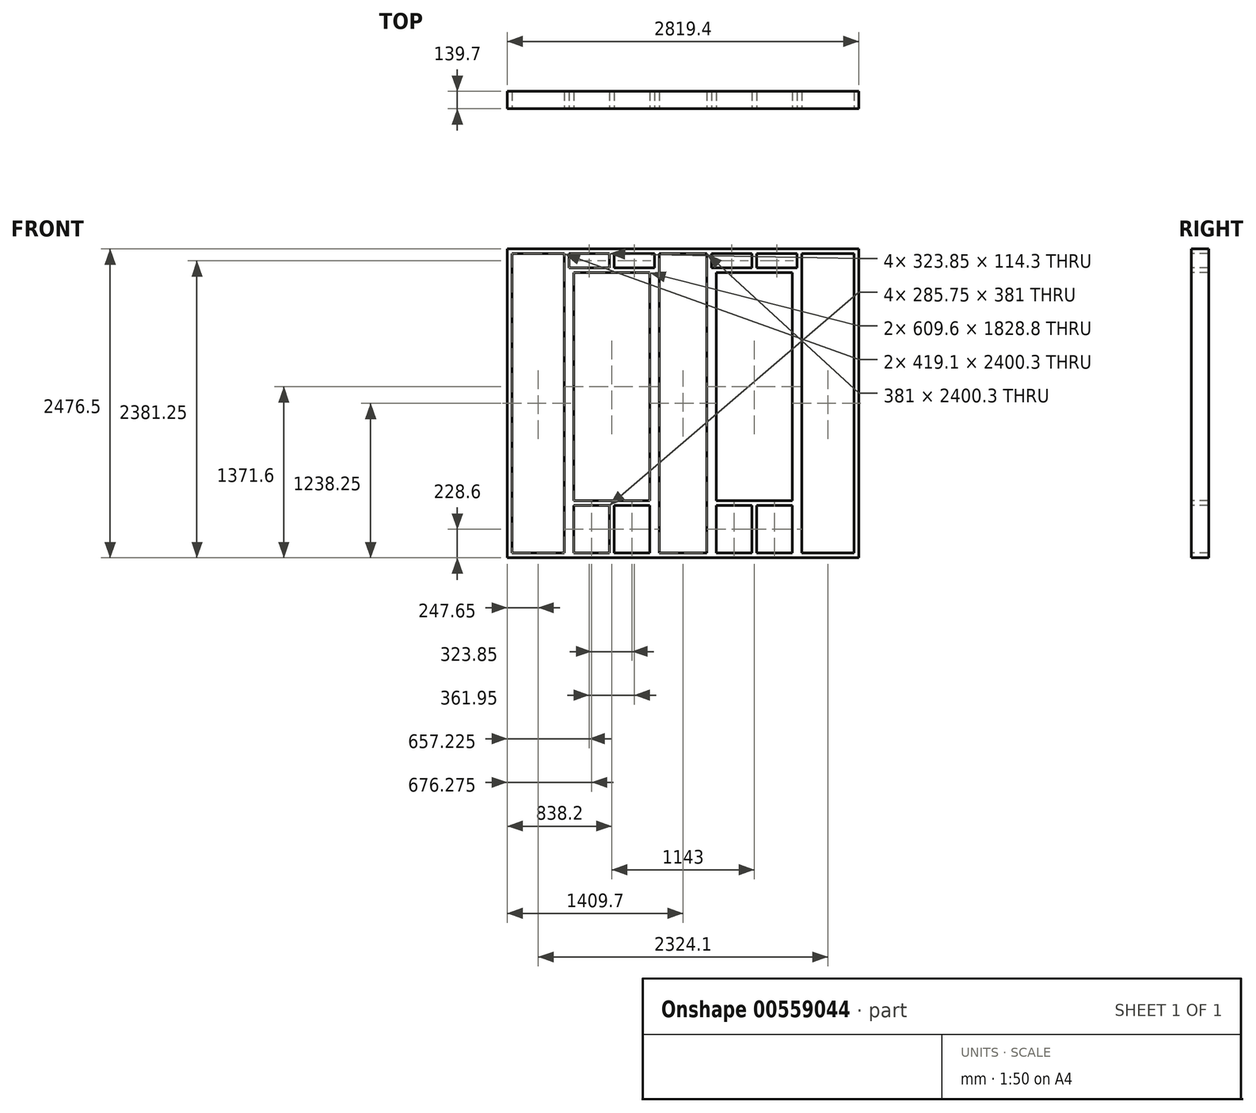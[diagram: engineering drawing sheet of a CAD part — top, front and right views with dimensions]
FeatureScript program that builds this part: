
annotation { "Feature Type Name" : "Feature", "Feature Type Description" : "" }
export const myFeature = defineFeature(function(context is Context, id is Id, definition is map)
    precondition{}
    {
        {
            var Q0;
            Q0=qCreatedBy(makeId("Front.planeOp"),FACE);
            var sketch = newSketch(context, id + "F0", { "sketchPlane" : qUnion([Q0])});
            skLineSegment(sketch, "E0.bottom", {"start": v(0, 0) * mm, "end": v(2819.4, 0) * mm});
            skLineSegment(sketch, "E0.top", {"start": v(0, 2476.5) * mm, "end": v(2819.4, 2476.5) * mm});
            skLineSegment(sketch, "E0.left", {"start": v(0, 0) * mm, "end": v(0, 2476.5) * mm});
            skLineSegment(sketch, "E0.right", {"start": v(2819.4, 0) * mm, "end": v(2819.4, 2476.5) * mm});
            skSolve(sketch);
        }
        {
            var Q0;
            Q0 = qSketchRegion(id + "F0", true);
            extrude(context, id + "F1", {"entities" : qUnion([Q0]), "depth" : 139.7 * mm, "offsetDistance" : 25.4 * mm});
        }
        {
            var Q0;
            Q0=makeQuery(id+"F1.opExtrude","CAP_FACE",FACE,{"disambiguationData":[OSD([sQuery(id+"F0.wireOp",EDGE,"E0.bottom"),sQuery(id+"F0.wireOp",EDGE,"E0.top"),sQuery(id+"F0.wireOp",EDGE,"E0.left"),sQuery(id+"F0.wireOp",EDGE,"E0.right")])],"isStart":false});
            var sketch = newSketch(context, id + "F2", { "sketchPlane" : qUnion([Q0])});
            skLineSegment(sketch, "E1.bottom", {"start": v(533.4, 457.2) * mm, "end": v(1143, 457.2) * mm});
            skLineSegment(sketch, "E1.top", {"start": v(533.4, 2286) * mm, "end": v(1143, 2286) * mm});
            skLineSegment(sketch, "E1.left", {"start": v(533.4, 457.2) * mm, "end": v(533.4, 2286) * mm});
            skLineSegment(sketch, "E1.right", {"start": v(1143, 457.2) * mm, "end": v(1143, 2286) * mm});
            skLineSegment(sketch, "E2.bottom", {"start": v(1676.4, 457.2) * mm, "end": v(2286, 457.2) * mm});
            skLineSegment(sketch, "E2.top", {"start": v(1676.4, 2286) * mm, "end": v(2286, 2286) * mm});
            skLineSegment(sketch, "E2.left", {"start": v(1676.4, 457.2) * mm, "end": v(1676.4, 2286) * mm});
            skLineSegment(sketch, "E2.right", {"start": v(2286, 457.2) * mm, "end": v(2286, 2286) * mm});
            skLineSegment(sketch, "E3", {"start": v(533.4, 2286) * mm, "end": v(0, 2286) * mm, "construction": true});
            skLineSegment(sketch, "E4", {"start": v(1143, 2286) * mm, "end": v(1676.4, 2286) * mm, "construction": true});
            skLineSegment(sketch, "E5", {"start": v(2286, 2286) * mm, "end": v(2819.4, 2286) * mm, "construction": true});
            skSolve(sketch);
        }
        {
            var Q0;
            Q0 = qSketchRegion(id + "F2", true);
            extrude(context, id + "F3", {"entities" : qUnion([Q0]), "operationType" : NewBodyOperationType.REMOVE, "endBound" : BoundingType.THROUGH_ALL, "oppositeDirection" : true, "depth" : 25.4 * mm, "offsetDistance" : 25.4 * mm});
        }
        {
            var Q0;
            Q0=makeQuery(id+"F1.opExtrude","CAP_FACE",FACE,{"disambiguationData":[OSD([sQuery(id+"F0.wireOp",EDGE,"E0.bottom"),sQuery(id+"F0.wireOp",EDGE,"E0.top"),sQuery(id+"F0.wireOp",EDGE,"E0.left"),sQuery(id+"F0.wireOp",EDGE,"E0.right")])],"isStart":false});
            var sketch = newSketch(context, id + "F4", { "sketchPlane" : qUnion([Q0])});
            skLineSegment(sketch, "E6.bottom", {"start": v(2781.3, 38.1) * mm, "end": v(2362.2, 38.1) * mm});
            skLineSegment(sketch, "E6.top", {"start": v(2781.3, 2438.4) * mm, "end": v(2362.2, 2438.4) * mm});
            skLineSegment(sketch, "E6.left", {"start": v(2781.3, 38.1) * mm, "end": v(2781.3, 2438.4) * mm});
            skLineSegment(sketch, "E6.right", {"start": v(2362.2, 38.1) * mm, "end": v(2362.2, 2438.4) * mm});
            skLineSegment(sketch, "E7.bottom", {"start": v(1600.2, 2438.4) * mm, "end": v(1219.2, 2438.4) * mm});
            skLineSegment(sketch, "E7.top", {"start": v(1600.2, 38.1) * mm, "end": v(1219.2, 38.1) * mm});
            skLineSegment(sketch, "E7.left", {"start": v(1600.2, 2438.4) * mm, "end": v(1600.2, 38.1) * mm});
            skLineSegment(sketch, "E7.right", {"start": v(1219.2, 2438.4) * mm, "end": v(1219.2, 38.1) * mm});
            skLineSegment(sketch, "E8.bottom", {"start": v(457.2, 2438.4) * mm, "end": v(38.1, 2438.4) * mm});
            skLineSegment(sketch, "E8.top", {"start": v(457.2, 38.1) * mm, "end": v(38.1, 38.1) * mm});
            skLineSegment(sketch, "E8.left", {"start": v(457.2, 2438.4) * mm, "end": v(457.2, 38.1) * mm});
            skLineSegment(sketch, "E8.right", {"start": v(38.1, 2438.4) * mm, "end": v(38.1, 38.1) * mm});
            skLineSegment(sketch, "E9.bottom", {"start": v(495.3, 2324.1) * mm, "end": v(819.15, 2324.1) * mm});
            skLineSegment(sketch, "E9.top", {"start": v(495.3, 2438.4) * mm, "end": v(819.15, 2438.4) * mm});
            skLineSegment(sketch, "E9.left", {"start": v(495.3, 2324.1) * mm, "end": v(495.3, 2438.4) * mm});
            skLineSegment(sketch, "E9.right", {"start": v(819.15, 2324.1) * mm, "end": v(819.15, 2438.4) * mm});
            skLineSegment(sketch, "E10.bottom", {"start": v(1181.1, 2324.1) * mm, "end": v(857.25, 2324.1) * mm});
            skLineSegment(sketch, "E10.top", {"start": v(1181.1, 2438.4) * mm, "end": v(857.25, 2438.4) * mm});
            skLineSegment(sketch, "E10.left", {"start": v(1181.1, 2324.1) * mm, "end": v(1181.1, 2438.4) * mm});
            skLineSegment(sketch, "E10.right", {"start": v(857.25, 2324.1) * mm, "end": v(857.25, 2438.4) * mm});
            skLineSegment(sketch, "E11.bottom", {"start": v(533.4, 38.1) * mm, "end": v(819.15, 38.1) * mm});
            skLineSegment(sketch, "E11.top", {"start": v(533.4, 419.1) * mm, "end": v(819.15, 419.1) * mm});
            skLineSegment(sketch, "E11.left", {"start": v(533.4, 38.1) * mm, "end": v(533.4, 419.1) * mm});
            skLineSegment(sketch, "E11.right", {"start": v(819.15, 38.1) * mm, "end": v(819.15, 419.1) * mm});
            skLineSegment(sketch, "E12.bottom", {"start": v(857.25, 38.1) * mm, "end": v(1143, 38.1) * mm});
            skLineSegment(sketch, "E12.top", {"start": v(857.25, 419.1) * mm, "end": v(1143, 419.1) * mm});
            skLineSegment(sketch, "E12.left", {"start": v(857.25, 38.1) * mm, "end": v(857.25, 419.1) * mm});
            skLineSegment(sketch, "E12.right", {"start": v(1143, 38.1) * mm, "end": v(1143, 419.1) * mm});
            skLineSegment(sketch, "E13.bottom", {"start": v(1638.3, 2324.1) * mm, "end": v(1962.15, 2324.1) * mm});
            skLineSegment(sketch, "E13.top", {"start": v(1638.3, 2438.4) * mm, "end": v(1962.15, 2438.4) * mm});
            skLineSegment(sketch, "E13.left", {"start": v(1638.3, 2324.1) * mm, "end": v(1638.3, 2438.4) * mm});
            skLineSegment(sketch, "E13.right", {"start": v(1962.15, 2324.1) * mm, "end": v(1962.15, 2438.4) * mm});
            skLineSegment(sketch, "E14.bottom", {"start": v(2324.1, 2324.1) * mm, "end": v(2000.25, 2324.1) * mm});
            skLineSegment(sketch, "E14.top", {"start": v(2324.1, 2438.4) * mm, "end": v(2000.25, 2438.4) * mm});
            skLineSegment(sketch, "E14.left", {"start": v(2324.1, 2324.1) * mm, "end": v(2324.1, 2438.4) * mm});
            skLineSegment(sketch, "E14.right", {"start": v(2000.25, 2324.1) * mm, "end": v(2000.25, 2438.4) * mm});
            skLineSegment(sketch, "E15.bottom", {"start": v(1676.4, 38.1) * mm, "end": v(1962.15, 38.1) * mm});
            skLineSegment(sketch, "E15.top", {"start": v(1676.4, 419.1) * mm, "end": v(1962.15, 419.1) * mm});
            skLineSegment(sketch, "E15.left", {"start": v(1676.4, 38.1) * mm, "end": v(1676.4, 419.1) * mm});
            skLineSegment(sketch, "E15.right", {"start": v(1962.15, 38.1) * mm, "end": v(1962.15, 419.1) * mm});
            skLineSegment(sketch, "E16.bottom", {"start": v(2286, 38.1) * mm, "end": v(2000.25, 38.1) * mm});
            skLineSegment(sketch, "E16.top", {"start": v(2286, 419.1) * mm, "end": v(2000.25, 419.1) * mm});
            skLineSegment(sketch, "E16.left", {"start": v(2286, 38.1) * mm, "end": v(2286, 419.1) * mm});
            skLineSegment(sketch, "E16.right", {"start": v(2000.25, 38.1) * mm, "end": v(2000.25, 419.1) * mm});
            skSolve(sketch);
        }
        {
            var Q0;
            Q0 = qSketchRegion(id + "F4", true);
            extrude(context, id + "F5", {"entities" : qUnion([Q0]), "operationType" : NewBodyOperationType.REMOVE, "endBound" : BoundingType.THROUGH_ALL, "oppositeDirection" : true, "depth" : 25.4 * mm, "offsetDistance" : 25.4 * mm});
        }
    });
